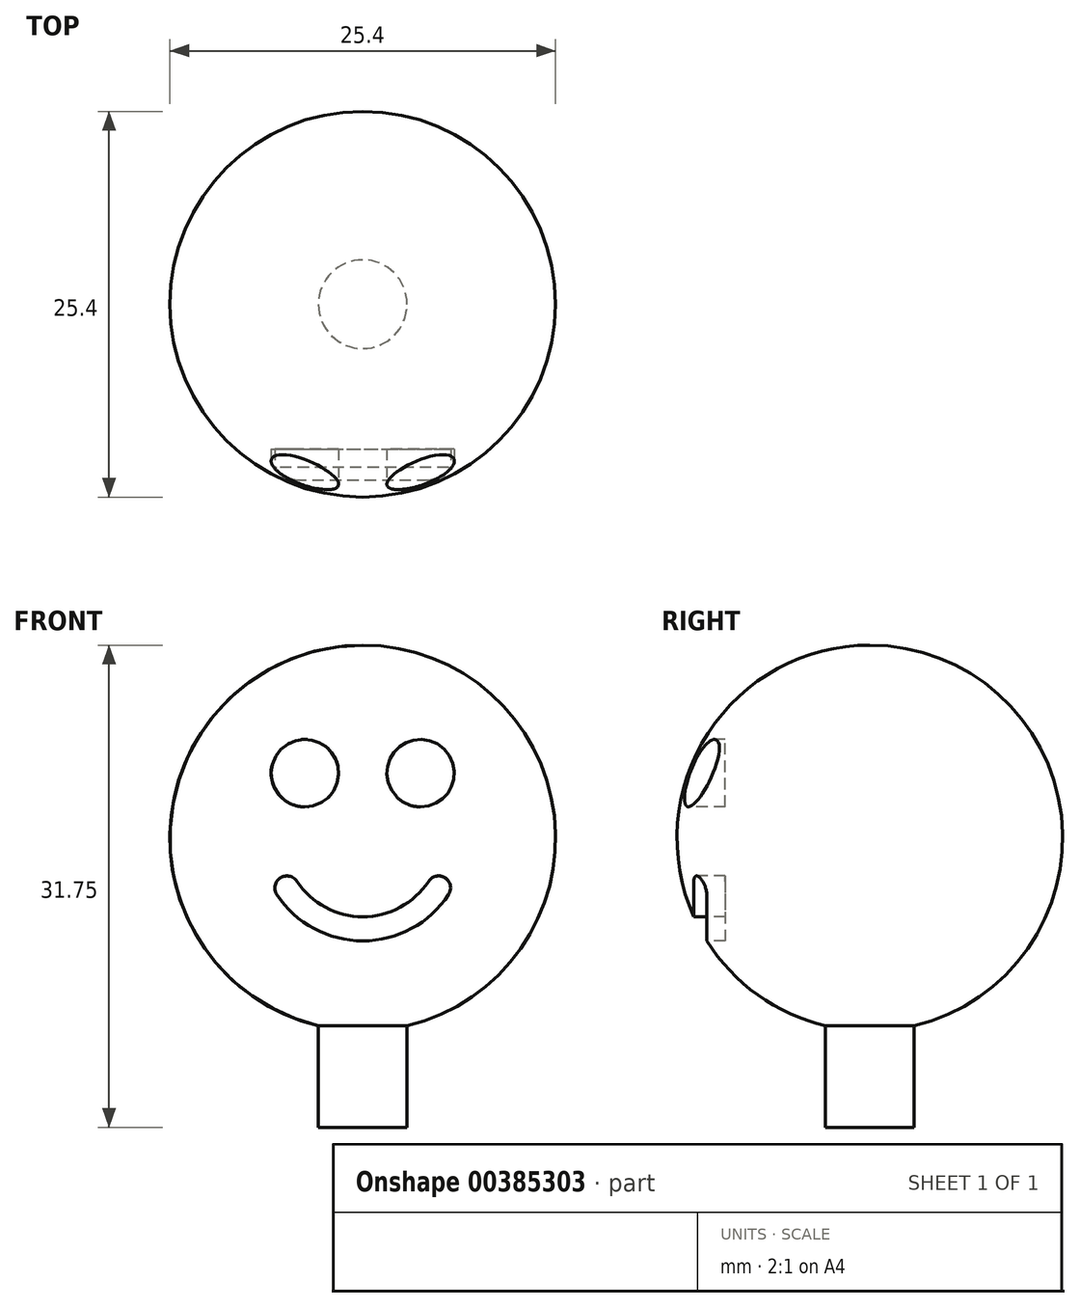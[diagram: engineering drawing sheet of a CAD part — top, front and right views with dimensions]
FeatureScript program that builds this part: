
annotation { "Feature Type Name" : "Feature", "Feature Type Description" : "" }
export const myFeature = defineFeature(function(context is Context, id is Id, definition is map)
    precondition{}
    {
        {
            var Q0;
            Q0=qCreatedBy(makeId("Front.planeOp"),FACE);
            var sketch = newSketch(context, id + "F0", { "sketchPlane" : qUnion([Q0])});
            skArc(sketch, "E0", {"start": v(0, -12.7) * mm, "mid": v(12.7, 0) * mm, "end": v(0, 12.7) * mm});
            skLineSegment(sketch, "E1", {"start": v(0, 0) * mm, "end": v(0, 12.7) * mm});
            skLineSegment(sketch, "E2", {"start": v(0, 0) * mm, "end": v(0, -12.7) * mm});
            skSolve(sketch);
        }
        {
            var Q0;
            Q0 = qSketchRegion(id + "F0", true);
            var Q1;
            Q1=sQuery(id+"F0.wireOp",EDGE,"E1");
            revolve(context, id + "F1", {"entities" : qUnion([Q0]), "axis" : qUnion([Q1]), "revolveType" : RevolveType.FULL});
        }
        {
            var Q0;
            Q0=qCreatedBy(makeId("Top.planeOp"),FACE);
            var sketch = newSketch(context, id + "F2", { "sketchPlane" : qUnion([Q0])});
            skCircle(sketch, "E3", {"center": v(0, 0) * mm, "radius": 2.92 * mm});
            skSolve(sketch);
        }
        {
            var Q0;
            Q0 = qSketchRegion(id + "F2", true);
            extrude(context, id + "F3", {"entities" : qUnion([Q0]), "operationType" : NewBodyOperationType.ADD, "oppositeDirection" : true, "depth" : 19.05 * mm});
        }
        {
            var Q0;
            Q0=qCreatedBy(makeId("Front.planeOp"),FACE);
            cPlane(context, id + "F4", {"entities" : qUnion([Q0]), "cplaneType" : CPlaneType.OFFSET, "offset" : 12.7 * mm, "width" : 152.4 * mm, "height" : 152.4 * mm});
        }
        {
            var Q0;
            Q0=qCreatedBy(id+"F4.planeOp",FACE);
            var sketch = newSketch(context, id + "F5", { "sketchPlane" : qUnion([Q0])});
            skCircle(sketch, "E4", {"center": v(-3.81, 4.27) * mm, "radius": 2.22 * mm});
            skCircle(sketch, "E5", {"center": v(3.81, 4.27) * mm, "radius": 2.22 * mm});
            skLineSegment(sketch, "E6", {"start": v(-3.81, 4.27) * mm, "end": v(3.81, 4.27) * mm, "construction": true});
            skPoint(sketch, "E7", {"position": v(0, 4.27) * mm});
            skArc(sketch, "E8", {"start": v(-5.66, -3.73) * mm, "mid": v(0, -6.78) * mm, "end": v(5.66, -3.73) * mm});
            skArc(sketch, "E9.0", {"start": v(-4.33, -2.86) * mm, "mid": v(0, -5.19) * mm, "end": v(4.33, -2.86) * mm});
            skArc(sketch, "E10", {"start": v(-4.33, -2.86) * mm, "mid": v(-5.43, -2.63) * mm, "end": v(-5.66, -3.73) * mm});
            skArc(sketch, "E11", {"start": v(5.66, -3.73) * mm, "mid": v(5.43, -2.63) * mm, "end": v(4.33, -2.86) * mm});
            skLineSegment(sketch, "E12", {"start": v(-5.66, -3.73) * mm, "end": v(-4.33, -2.86) * mm, "construction": true});
            skLineSegment(sketch, "E13", {"start": v(4.33, -2.86) * mm, "end": v(5.66, -3.73) * mm, "construction": true});
            skSolve(sketch);
        }
        {
            var Q0;
            Q0 = qSketchRegion(id + "F5", true);
            extrude(context, id + "F6", {"entities" : qUnion([Q0]), "operationType" : NewBodyOperationType.REMOVE, "oppositeDirection" : true, "depth" : 3.17 * mm});
        }
    });
